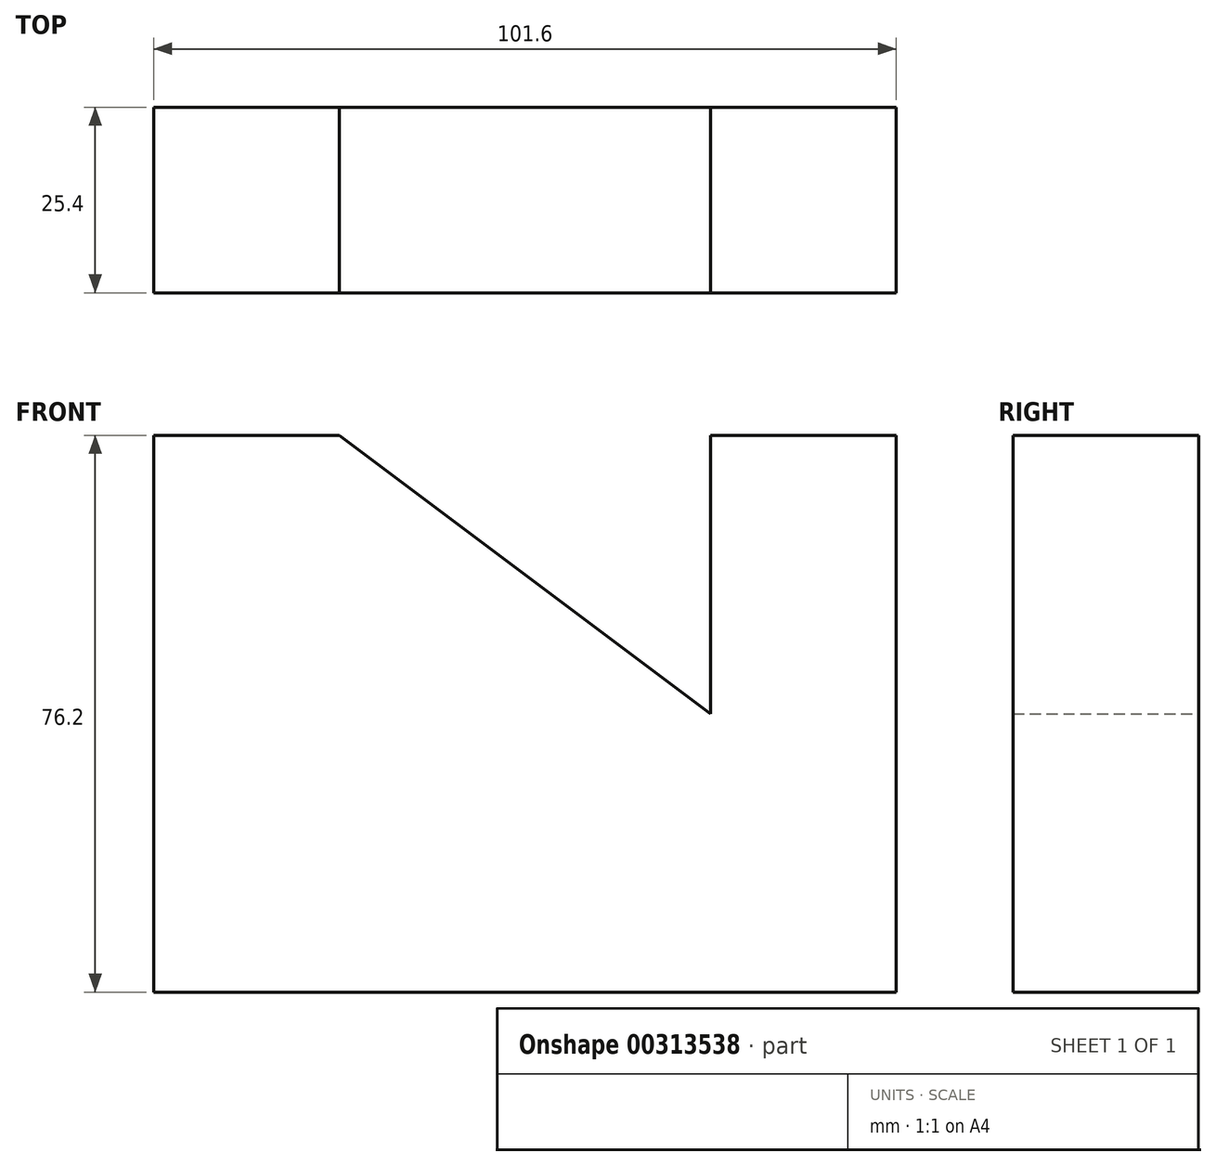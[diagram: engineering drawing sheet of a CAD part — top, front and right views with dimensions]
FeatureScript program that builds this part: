
annotation { "Feature Type Name" : "Feature", "Feature Type Description" : "" }
export const myFeature = defineFeature(function(context is Context, id is Id, definition is map)
    precondition{}
    {
        {
            var Q0;
            Q0=qCreatedBy(makeId("Front.planeOp"),FACE);
            var sketch = newSketch(context, id + "F0", { "sketchPlane" : qUnion([Q0])});
            skLineSegment(sketch, "E0", {"start": v(-62.02, 10.4) * mm, "end": v(-62.02, -65.8) * mm});
            skLineSegment(sketch, "E1", {"start": v(-62.02, -65.8) * mm, "end": v(39.58, -65.8) * mm});
            skLineSegment(sketch, "E2", {"start": v(39.58, -65.8) * mm, "end": v(39.58, 10.4) * mm});
            skLineSegment(sketch, "E3", {"start": v(-62.02, 10.4) * mm, "end": v(-36.62, 10.4) * mm});
            skLineSegment(sketch, "E4", {"start": v(39.58, 10.4) * mm, "end": v(14.18, 10.4) * mm});
            skPoint(sketch, "E5.startSnap0", {"position": v(-11.22, -65.8) * mm});
            skLineSegment(sketch, "E6", {"start": v(14.18, -27.7) * mm, "end": v(14.18, 10.4) * mm});
            skLineSegment(sketch, "E7", {"start": v(-36.62, 10.4) * mm, "end": v(14.18, -27.7) * mm});
            skSolve(sketch);
        }
        {
            var Q0;
            Q0 = qSketchRegion(id + "F0", true);
            extrude(context, id + "F1", {"entities" : qUnion([Q0]), "depth" : 25.4 * mm});
        }
    });
